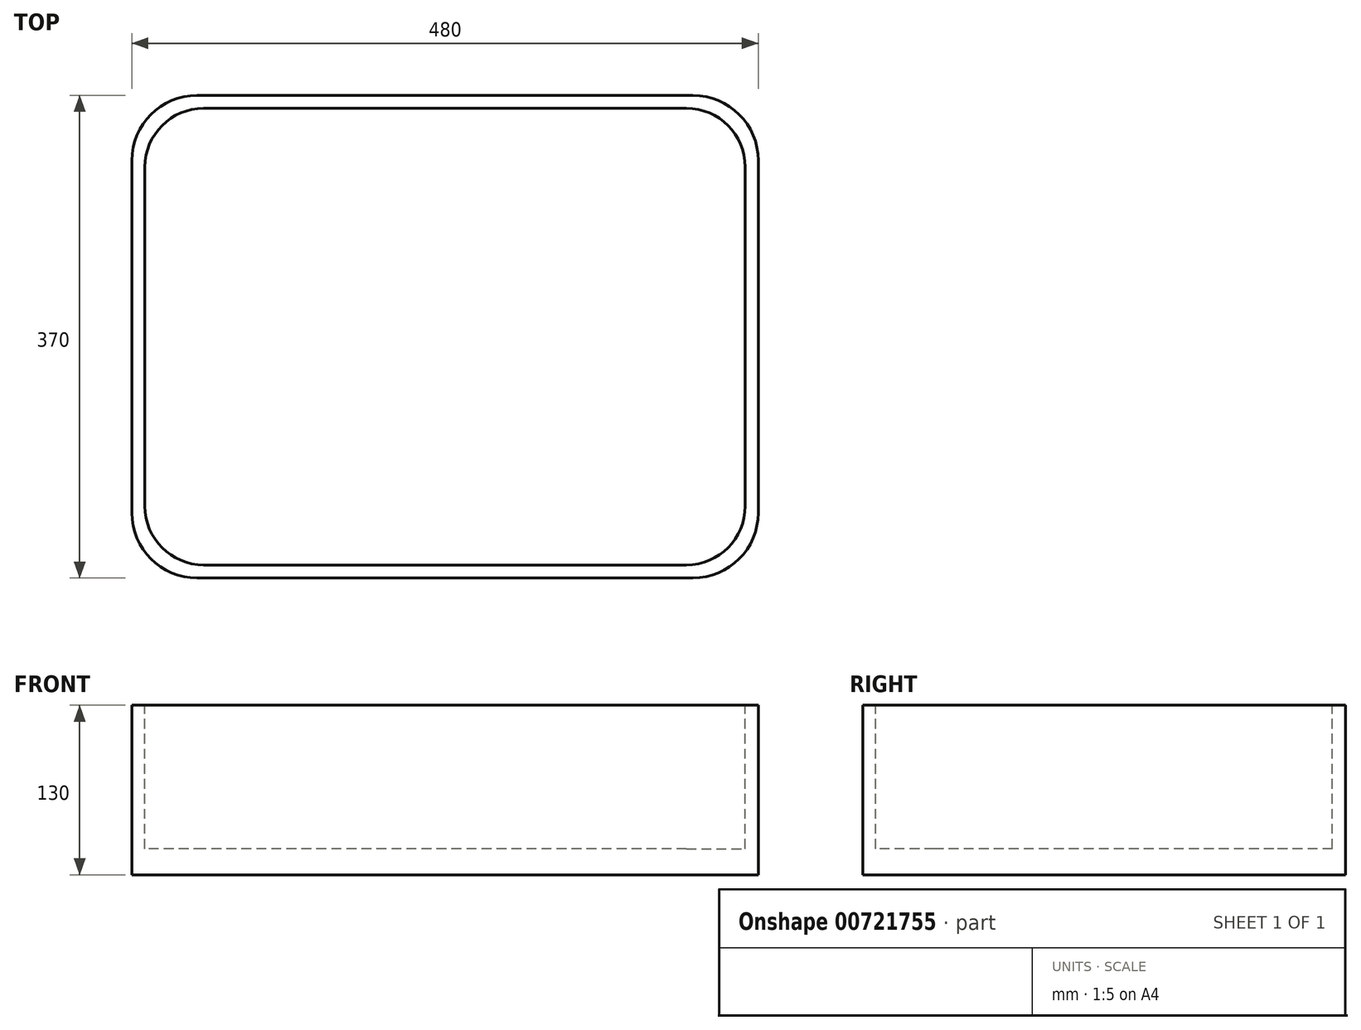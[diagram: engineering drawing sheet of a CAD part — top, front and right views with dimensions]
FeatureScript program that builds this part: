
annotation { "Feature Type Name" : "Feature", "Feature Type Description" : "" }
export const myFeature = defineFeature(function(context is Context, id is Id, definition is map)
    precondition{}
    {
        {
            var Q0;
            Q0=qCreatedBy(makeId("Top.planeOp"),FACE);
            var sketch = newSketch(context, id + "F0", { "sketchPlane" : qUnion([Q0])});
            skLineSegment(sketch, "E0.bottom", {"start": v(240, 185) * mm, "end": v(-240, 185) * mm});
            skLineSegment(sketch, "E0.top", {"start": v(240, -185) * mm, "end": v(-240, -185) * mm});
            skLineSegment(sketch, "E0.left", {"start": v(240, 185) * mm, "end": v(240, -185) * mm});
            skLineSegment(sketch, "E0.right", {"start": v(-240, 185) * mm, "end": v(-240, -185) * mm});
            skPoint(sketch, "E0.middle", {"position": v(0, 0) * mm});
            skSolve(sketch);
        }
        {
            var Q0;
            Q0=makeQuery(id+"F0.imprint","IMPRINT",FACE,{"disambiguationData":[TD([[makeQuery(id+"F0.imprint","IMPRINT",EDGE,{"derivedFrom":sQuery(id+"F0.wireOp",EDGE,"E0.bottom")}),1.0]])]});
            extrude(context, id + "F1", {"entities" : qUnion([Q0]), "depth" : 130 * mm, "offsetDistance" : 25 * mm});
        }
        {
            var Q0;
            Q0=makeQuery(id+"F1.opExtrude","SWEPT_EDGE",EDGE,{"disambiguationData":[OSD([sQuery(id+"F0.wireOp",EDGE,"E0.top"),sQuery(id+"F0.wireOp",EDGE,"E0.left")])]});
            var Q1;
            Q1=makeQuery(id+"F1.opExtrude","SWEPT_EDGE",EDGE,{"disambiguationData":[OSD([sQuery(id+"F0.wireOp",EDGE,"E0.top"),sQuery(id+"F0.wireOp",EDGE,"E0.right")])]});
            var Q2;
            Q2=makeQuery(id+"F1.opExtrude","SWEPT_EDGE",EDGE,{"disambiguationData":[OSD([sQuery(id+"F0.wireOp",EDGE,"E0.bottom"),sQuery(id+"F0.wireOp",EDGE,"E0.left")])]});
            var Q3;
            Q3=makeQuery(id+"F1.opExtrude","SWEPT_EDGE",EDGE,{"disambiguationData":[OSD([sQuery(id+"F0.wireOp",EDGE,"E0.bottom"),sQuery(id+"F0.wireOp",EDGE,"E0.right")])]});
            fillet(context, id + "F2", {"entities" : qUnion([Q0, Q1, Q2, Q3]), "radius" : 50 * mm, "tangentPropagation" : true, "allowEdgeOverflow" : false});
        }
        {
            var Q0;
            Q0=makeQuery(id+"F1.opExtrude","CAP_FACE",FACE,{"disambiguationData":[OSD([sQuery(id+"F0.wireOp",EDGE,"E0.bottom"),sQuery(id+"F0.wireOp",EDGE,"E0.top"),sQuery(id+"F0.wireOp",EDGE,"E0.left"),sQuery(id+"F0.wireOp",EDGE,"E0.right")])],"isStart":false});
            var sketch = newSketch(context, id + "F3", { "sketchPlane" : qUnion([Q0])});
            skLineSegment(sketch, "E1.bottom", {"start": v(185, 175) * mm, "end": v(-185, 175) * mm});
            skLineSegment(sketch, "E1.top", {"start": v(185, -175) * mm, "end": v(-185, -175) * mm});
            skLineSegment(sketch, "E1.left", {"start": v(230, 130) * mm, "end": v(230, -130) * mm});
            skLineSegment(sketch, "E1.right", {"start": v(-230, 130) * mm, "end": v(-230, -130) * mm});
            skPoint(sketch, "E1.middle", {"position": v(0, 0) * mm});
            skPoint(sketch, "E2.visualSharp", {"position": v(-230, -175) * mm});
            skArc(sketch, "E2.filletArc", {"start": v(-230, -130) * mm, "mid": v(-216.82, -161.82) * mm, "end": v(-185, -175) * mm});
            skPoint(sketch, "E3.visualSharp", {"position": v(-230, 175) * mm});
            skArc(sketch, "E3.filletArc", {"start": v(-185, 175) * mm, "mid": v(-216.82, 161.82) * mm, "end": v(-230, 130) * mm});
            skPoint(sketch, "E4.visualSharp", {"position": v(230, 175) * mm});
            skArc(sketch, "E4.filletArc", {"start": v(230, 130) * mm, "mid": v(216.82, 161.82) * mm, "end": v(185, 175) * mm});
            skPoint(sketch, "E5.visualSharp", {"position": v(230, -175) * mm});
            skArc(sketch, "E5.filletArc", {"start": v(185, -175) * mm, "mid": v(216.82, -161.82) * mm, "end": v(230, -130) * mm});
            skSolve(sketch);
        }
        {
            var Q0;
            Q0=makeQuery(id+"F3.imprint","IMPRINT",FACE,{"disambiguationData":[TD([[makeQuery(id+"F3.imprint","IMPRINT",EDGE,{"derivedFrom":sQuery(id+"F3.wireOp",EDGE,"E1.bottom")}),1.0]])]});
            extrude(context, id + "F4", {"entities" : qUnion([Q0]), "operationType" : NewBodyOperationType.REMOVE, "oppositeDirection" : true, "depth" : 110 * mm, "offsetDistance" : 25 * mm});
        }
    });
